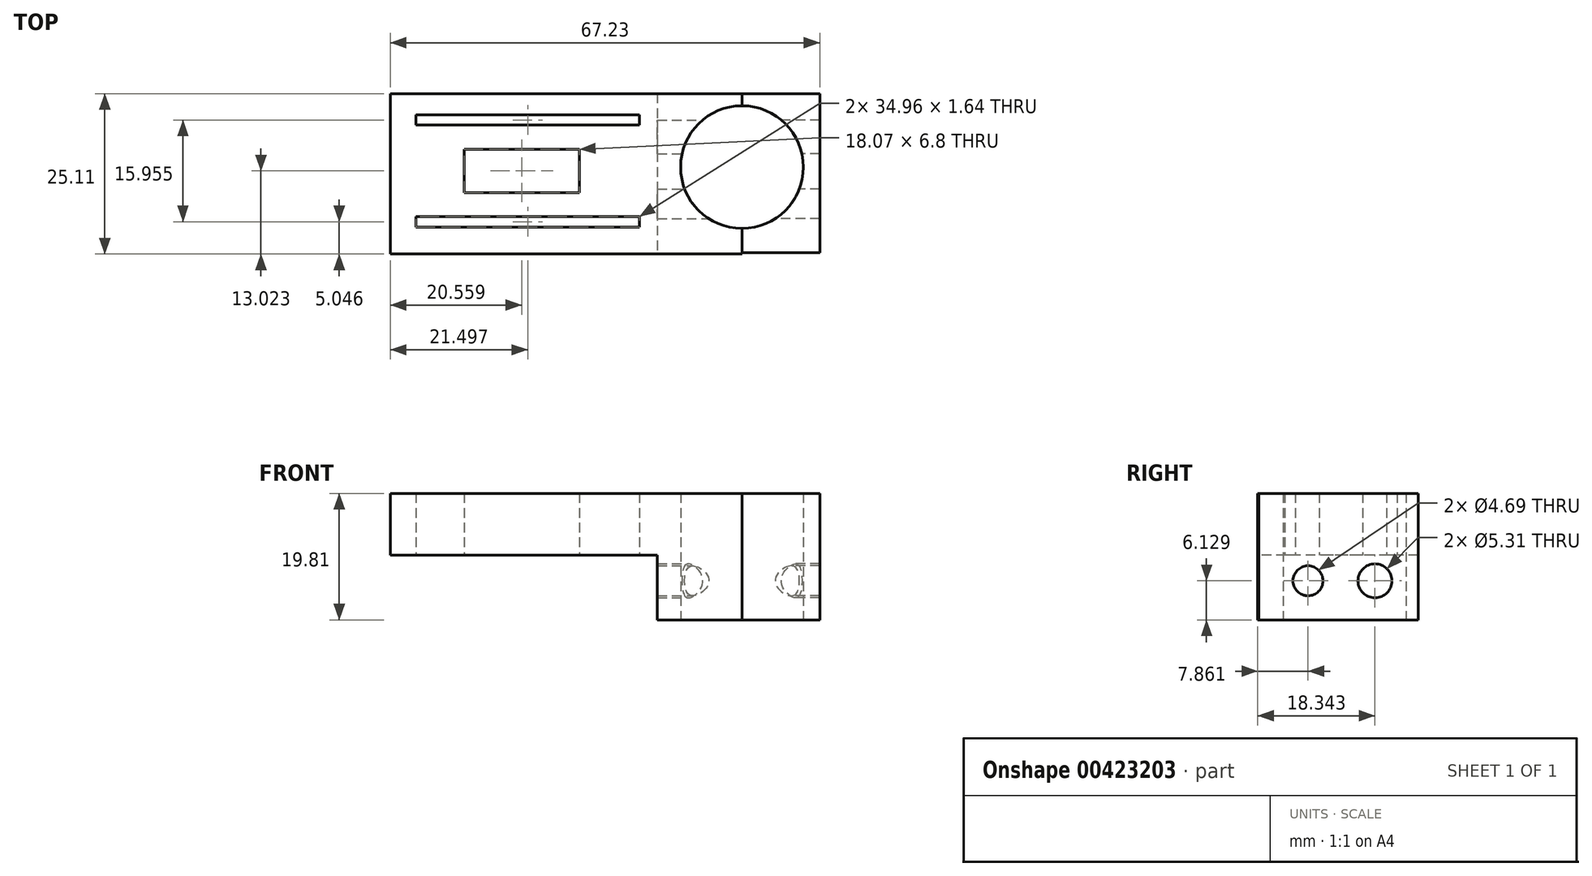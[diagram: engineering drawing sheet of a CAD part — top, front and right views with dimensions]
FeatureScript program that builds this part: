
annotation { "Feature Type Name" : "Feature", "Feature Type Description" : "" }
export const myFeature = defineFeature(function(context is Context, id is Id, definition is map)
    precondition{}
    {
        {
            var Q0;
            Q0=qCreatedBy(makeId("Top.planeOp"),FACE);
            var sketch = newSketch(context, id + "F0", { "sketchPlane" : qUnion([Q0])});
            skLineSegment(sketch, "E0.bottom", {"start": v(-55.05, 11.5) * mm, "end": v(0, 11.5) * mm});
            skLineSegment(sketch, "E0.top", {"start": v(-55.05, -13.6) * mm, "end": v(0, -13.6) * mm});
            skLineSegment(sketch, "E0.left", {"start": v(-55.05, 11.5) * mm, "end": v(-55.05, -13.6) * mm});
            skLineSegment(sketch, "E0.right", {"start": v(0, 11.5) * mm, "end": v(0, -13.6) * mm});
            skLineSegment(sketch, "E1.bottom", {"start": v(0.02, 11.5) * mm, "end": v(12.18, 11.5) * mm});
            skLineSegment(sketch, "E1.top", {"start": v(0.02, -13.42) * mm, "end": v(12.18, -13.42) * mm});
            skLineSegment(sketch, "E1.left", {"start": v(0.02, 11.5) * mm, "end": v(0.02, -13.42) * mm});
            skLineSegment(sketch, "E1.right", {"start": v(12.18, 11.5) * mm, "end": v(12.18, -13.42) * mm});
            skSolve(sketch);
        }
        {
            var Q0;
            Q0 = qSketchRegion(id + "F0", true);
            extrude(context, id + "F1", {"entities" : qUnion([Q0]), "depth" : 19.8 * mm});
        }
        {
            var Q0;
            Q0=qCreatedBy(makeId("Top.planeOp"),FACE);
            var sketch = newSketch(context, id + "F2", { "sketchPlane" : qUnion([Q0])});
            skCircle(sketch, "E2", {"center": v(0, 0) * mm, "radius": 9.6 * mm});
            skSolve(sketch);
        }
        {
            var Q0;
            Q0 = qSketchRegion(id + "F2", true);
            extrude(context, id + "F3", {"entities" : qUnion([Q0]), "operationType" : NewBodyOperationType.REMOVE, "depth" : 37.34 * mm});
        }
        {
            var Q0;
            Q0=qCreatedBy(makeId("Top.planeOp"),FACE);
            var sketch = newSketch(context, id + "F4", { "sketchPlane" : qUnion([Q0])});
            skLineSegment(sketch, "E3.bottom", {"start": v(-64.17, 15.72) * mm, "end": v(-13.26, 15.72) * mm});
            skLineSegment(sketch, "E3.top", {"start": v(-64.17, -16.66) * mm, "end": v(-13.26, -16.66) * mm});
            skLineSegment(sketch, "E3.left", {"start": v(-64.17, 15.72) * mm, "end": v(-64.17, -16.66) * mm});
            skLineSegment(sketch, "E3.right", {"start": v(-13.26, 15.72) * mm, "end": v(-13.26, -16.66) * mm});
            skSolve(sketch);
        }
        {
            var Q0;
            Q0 = qSketchRegion(id + "F4", true);
            extrude(context, id + "F5", {"entities" : qUnion([Q0]), "operationType" : NewBodyOperationType.REMOVE, "depth" : 10.16 * mm});
        }
        {
            var Q0;
            Q0=qCreatedBy(makeId("Right.planeOp"),FACE);
            var sketch = newSketch(context, id + "F6", { "sketchPlane" : qUnion([Q0])});
            skCircle(sketch, "E4", {"center": v(4.73, 6.13) * mm, "radius": 2.65 * mm});
            skCircle(sketch, "E5", {"center": v(-5.75, 6.13) * mm, "radius": 2.35 * mm});
            skSolve(sketch);
        }
        {
            var Q0;
            Q0 = qSketchRegion(id + "F6", true);
            extrude(context, id + "F7", {"entities" : qUnion([Q0]), "operationType" : NewBodyOperationType.REMOVE, "oppositeDirection" : true, "depth" : 25.4 * mm});
        }
        {
            var Q0;
            Q0 = qSketchRegion(id + "F6", true);
            extrude(context, id + "F8", {"entities" : qUnion([Q0]), "operationType" : NewBodyOperationType.REMOVE, "depth" : 29.2 * mm});
        }
        {
            var Q0;
            Q0=qCreatedBy(makeId("Top.planeOp"),FACE);
            var sketch = newSketch(context, id + "F9", { "sketchPlane" : qUnion([Q0])});
            skLineSegment(sketch, "E6.bottom", {"start": v(-51.03, -9.39) * mm, "end": v(-16.07, -9.39) * mm});
            skLineSegment(sketch, "E6.top", {"start": v(-51.03, -7.74) * mm, "end": v(-16.07, -7.74) * mm});
            skLineSegment(sketch, "E6.left", {"start": v(-51.03, -9.39) * mm, "end": v(-51.03, -7.74) * mm});
            skLineSegment(sketch, "E6.right", {"start": v(-16.07, -9.39) * mm, "end": v(-16.07, -7.74) * mm});
            skLineSegment(sketch, "E7.bottom", {"start": v(-51.03, 6.57) * mm, "end": v(-16.07, 6.57) * mm});
            skLineSegment(sketch, "E7.top", {"start": v(-51.03, 8.21) * mm, "end": v(-16.07, 8.21) * mm});
            skLineSegment(sketch, "E7.left", {"start": v(-51.03, 6.57) * mm, "end": v(-51.03, 8.21) * mm});
            skLineSegment(sketch, "E7.right", {"start": v(-16.07, 6.57) * mm, "end": v(-16.07, 8.21) * mm});
            skLineSegment(sketch, "E8.bottom", {"start": v(-43.52, -3.99) * mm, "end": v(-25.46, -3.99) * mm});
            skLineSegment(sketch, "E8.top", {"start": v(-43.52, 2.82) * mm, "end": v(-25.46, 2.82) * mm});
            skLineSegment(sketch, "E8.left", {"start": v(-43.52, -3.99) * mm, "end": v(-43.52, 2.82) * mm});
            skLineSegment(sketch, "E8.right", {"start": v(-25.46, -3.99) * mm, "end": v(-25.46, 2.82) * mm});
            skSolve(sketch);
        }
        {
            var Q0;
            Q0 = qSketchRegion(id + "F9", true);
            extrude(context, id + "F10", {"entities" : qUnion([Q0]), "operationType" : NewBodyOperationType.REMOVE, "depth" : 47.5 * mm});
        }
    });
